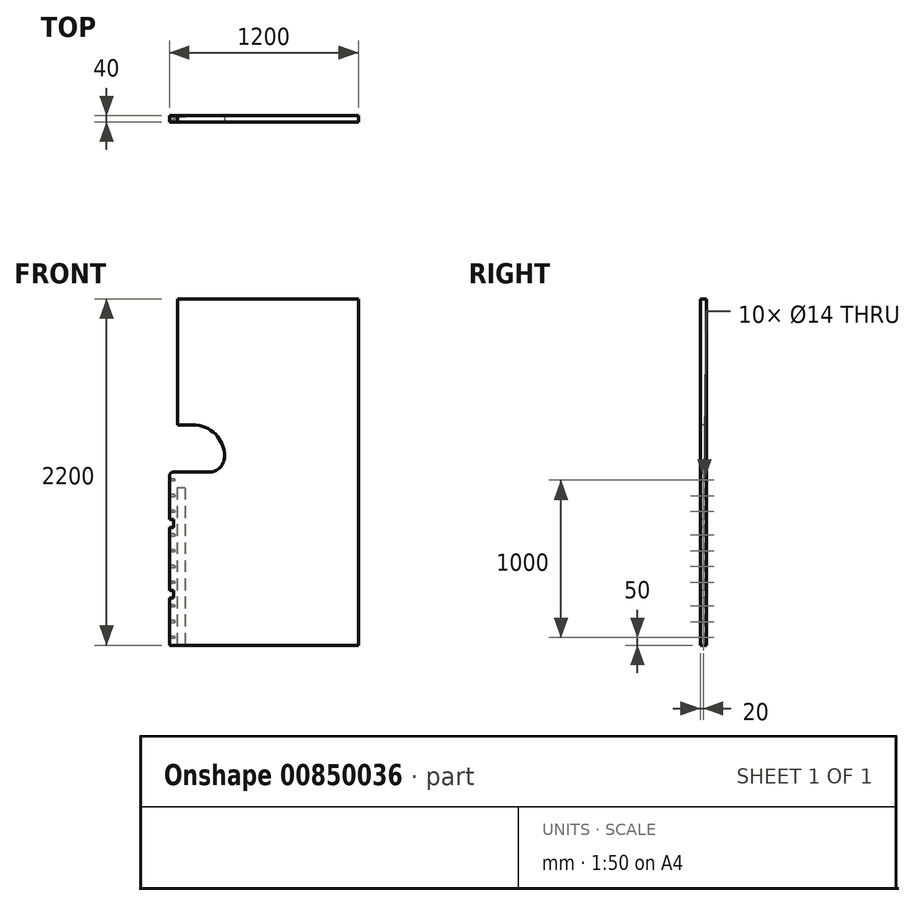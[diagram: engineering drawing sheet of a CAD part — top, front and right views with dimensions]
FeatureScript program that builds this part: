
annotation { "Feature Type Name" : "Feature", "Feature Type Description" : "" }
export const myFeature = defineFeature(function(context is Context, id is Id, definition is map)
    precondition{}
    {
        {
            var Q0;
            Q0=qCreatedBy(makeId("Front.planeOp"),FACE);
            var sketch = newSketch(context, id + "F0", { "sketchPlane" : qUnion([Q0])});
            skLineSegment(sketch, "E0.bottom", {"start": v(600, 1100) * mm, "end": v(-600, 1100) * mm});
            skLineSegment(sketch, "E0.top", {"start": v(600, -1100) * mm, "end": v(-600, -1100) * mm});
            skLineSegment(sketch, "E0.left", {"start": v(600, 1100) * mm, "end": v(600, -1100) * mm});
            skLineSegment(sketch, "E0.right", {"start": v(-600, 1100) * mm, "end": v(-600, -1100) * mm});
            skPoint(sketch, "E0.middle", {"position": v(0, 0) * mm});
            skSolve(sketch);
        }
        {
            var Q0;
            Q0=makeQuery(id+"F0.imprint","IMPRINT",FACE,{"disambiguationData":[TD([[makeQuery(id+"F0.imprint","IMPRINT",EDGE,{"derivedFrom":sQuery(id+"F0.wireOp",EDGE,"E0.bottom")}),1.0]])]});
            extrude(context, id + "F1", {"entities" : qUnion([Q0]), "depth" : 40 * mm, "offsetDistance" : 25 * mm});
        }
        {
            var Q0;
            Q0=makeQuery(id+"F1.opExtrude","CAP_FACE",FACE,{"disambiguationData":[OSD([sQuery(id+"F0.wireOp",EDGE,"E0.bottom"),sQuery(id+"F0.wireOp",EDGE,"E0.top"),sQuery(id+"F0.wireOp",EDGE,"E0.left"),sQuery(id+"F0.wireOp",EDGE,"E0.right")])],"isStart":true});
            var sketch = newSketch(context, id + "F2", { "sketchPlane" : qUnion([Q0])});
            skLineSegment(sketch, "E1.bottom", {"start": v(500, -100) * mm, "end": v(550, -100) * mm});
            skLineSegment(sketch, "E1.top", {"start": v(500, -1100) * mm, "end": v(550, -1100) * mm});
            skLineSegment(sketch, "E1.left", {"start": v(500, -100) * mm, "end": v(500, -1100) * mm});
            skLineSegment(sketch, "E1.right", {"start": v(550, -100) * mm, "end": v(550, -1100) * mm});
            skPoint(sketch, "E2.visualSharp", {"position": v(500, -100) * mm});
            skPoint(sketch, "E3.visualSharp", {"position": v(550, -100) * mm});
            skSolve(sketch);
        }
        {
            var Q0;
            Q0=makeQuery(id+"F2.imprint","IMPRINT",FACE,{"disambiguationData":[TD([[makeQuery(id+"F2.imprint","IMPRINT",EDGE,{"derivedFrom":sQuery(id+"F2.wireOp",EDGE,"E1.bottom")}),-1.0]])]});
            extrude(context, id + "F3", {"entities" : qUnion([Q0]), "operationType" : NewBodyOperationType.REMOVE, "oppositeDirection" : true, "depth" : 10 * mm, "offsetDistance" : 25 * mm});
        }
        {
            var Q0;
            Q0=makeQuery(id+"F1.opExtrude","CAP_FACE",FACE,{"disambiguationData":[OSD([sQuery(id+"F0.wireOp",EDGE,"E0.bottom"),sQuery(id+"F0.wireOp",EDGE,"E0.top"),sQuery(id+"F0.wireOp",EDGE,"E0.left"),sQuery(id+"F0.wireOp",EDGE,"E0.right")])],"isStart":false});
            var sketch = newSketch(context, id + "F4", { "sketchPlane" : qUnion([Q0])});
            skLineSegment(sketch, "E4", {"start": v(-600, 0) * mm, "end": v(-350, 0) * mm});
            skLineSegment(sketch, "E5", {"start": v(-450, 300) * mm, "end": v(-600, 300) * mm});
            skLineSegment(sketch, "E6", {"start": v(-600, 300) * mm, "end": v(-600, 0) * mm});
            skLineSegment(sketch, "E7", {"start": v(-250, 100) * mm, "end": v(-250, 100) * mm});
            skPoint(sketch, "E8.visualSharp", {"position": v(-250, 0) * mm});
            skArc(sketch, "E8.filletArc", {"start": v(-350, 0) * mm, "mid": v(-279.29, 29.29) * mm, "end": v(-250, 100) * mm});
            skPoint(sketch, "E9.visualSharp", {"position": v(-250, 300) * mm});
            skArc(sketch, "E9.filletArc", {"start": v(-250, 100) * mm, "mid": v(-308.58, 241.42) * mm, "end": v(-450, 300) * mm});
            skSolve(sketch);
        }
        {
            var Q0;
            Q0=makeQuery(id+"F4.imprint","IMPRINT",FACE,{"disambiguationData":[TD([[makeQuery(id+"F4.imprint","IMPRINT",EDGE,{"derivedFrom":sQuery(id+"F4.wireOp",EDGE,"E5")}),1.0]])]});
            extrude(context, id + "F5", {"entities" : qUnion([Q0]), "operationType" : NewBodyOperationType.REMOVE, "endBound" : BoundingType.THROUGH_ALL, "oppositeDirection" : true, "depth" : 25 * mm, "offsetDistance" : 25 * mm});
        }
        {
            var Q0;
            Q0=makeQuery(id+"F5.boolean.opBoolean","COPY",EDGE,{"derivedFrom":makeQuery(id+"F5.opExtrude","SWEPT_EDGE",EDGE,{"disambiguationData":[OSD([sQuery(id+"F0.wireOp",EDGE,"E0.right"),sQuery(id+"F4.wireOp",EDGE,"E5"),sQuery(id+"F4.wireOp",EDGE,"E6")])]})});
            var Q1;
            Q1=makeQuery(id+"F5.boolean.opBoolean","COPY",EDGE,{"derivedFrom":makeQuery(id+"F5.opExtrude","SWEPT_EDGE",EDGE,{"disambiguationData":[OSD([sQuery(id+"F0.wireOp",EDGE,"E0.right"),sQuery(id+"F4.wireOp",EDGE,"E4"),sQuery(id+"F4.wireOp",EDGE,"E6")])]})});
            fillet(context, id + "F6", {"entities" : qUnion([Q0, Q1]), "radius" : 25 * mm, "tangentPropagation" : true, "allowEdgeOverflow" : false});
        }
        {
            var Q0;
            Q0=makeQuery(id+"F1.opExtrude","CAP_FACE",FACE,{"disambiguationData":[OSD([sQuery(id+"F0.wireOp",EDGE,"E0.bottom"),sQuery(id+"F0.wireOp",EDGE,"E0.top"),sQuery(id+"F0.wireOp",EDGE,"E0.left"),sQuery(id+"F0.wireOp",EDGE,"E0.right")])],"isStart":false});
            var sketch = newSketch(context, id + "F7", { "sketchPlane" : qUnion([Q0])});
            skLineSegment(sketch, "E10.bottom", {"start": v(-600, 1100) * mm, "end": v(-549.1, 1100) * mm});
            skLineSegment(sketch, "E10.top", {"start": v(-600, 293.93) * mm, "end": v(-549.1, 293.93) * mm});
            skLineSegment(sketch, "E10.left", {"start": v(-600, 1100) * mm, "end": v(-600, 293.93) * mm});
            skLineSegment(sketch, "E10.right", {"start": v(-549.1, 1100) * mm, "end": v(-549.1, 293.93) * mm});
            skSolve(sketch);
        }
        {
            var Q0;
            {var subQ1=sQuery(id+"F7.wireOp",EDGE,"E10.bottom");Q0=makeQuery(id+"F7.imprint","IMPRINT",FACE,{"disambiguationData":[TD([[makeQuery(id+"F7.imprint","IMPRINT",EDGE,{"derivedFrom":subQ1}),1.0]])]});}
            extrude(context, id + "F8", {"entities" : qUnion([Q0]), "operationType" : NewBodyOperationType.REMOVE, "endBound" : BoundingType.THROUGH_ALL, "oppositeDirection" : true, "depth" : 25 * mm, "offsetDistance" : 25 * mm});
        }
        {
            var Q0;
            Q0=makeQuery(id+"F1.opExtrude","CAP_FACE",FACE,{"disambiguationData":[OSD([sQuery(id+"F0.wireOp",EDGE,"E0.bottom"),sQuery(id+"F0.wireOp",EDGE,"E0.top"),sQuery(id+"F0.wireOp",EDGE,"E0.left"),sQuery(id+"F0.wireOp",EDGE,"E0.right")])],"isStart":false});
            var sketch = newSketch(context, id + "F9", { "sketchPlane" : qUnion([Q0])});
            skLineSegment(sketch, "E11.bottom", {"start": v(-600, -300) * mm, "end": v(-575, -300) * mm});
            skLineSegment(sketch, "E11.top", {"start": v(-600, -350) * mm, "end": v(-575, -350) * mm});
            skLineSegment(sketch, "E11.left", {"start": v(-600, -300) * mm, "end": v(-600, -350) * mm});
            skLineSegment(sketch, "E11.right", {"start": v(-575, -300) * mm, "end": v(-575, -350) * mm});
            skLineSegment(sketch, "E12.bottom", {"start": v(-600, -750) * mm, "end": v(-575, -750) * mm});
            skLineSegment(sketch, "E12.top", {"start": v(-600, -800) * mm, "end": v(-575, -800) * mm});
            skLineSegment(sketch, "E12.left", {"start": v(-600, -750) * mm, "end": v(-600, -800) * mm});
            skLineSegment(sketch, "E12.right", {"start": v(-575, -750) * mm, "end": v(-575, -800) * mm});
            skSolve(sketch);
        }
        {
            var Q0;
            Q0=makeQuery(id+"F9.imprint","IMPRINT",FACE,{"disambiguationData":[TD([[makeQuery(id+"F9.imprint","IMPRINT",EDGE,{"derivedFrom":sQuery(id+"F9.wireOp",EDGE,"E11.bottom")}),-1.0]])]});
            var Q1;
            Q1=makeQuery(id+"F9.imprint","IMPRINT",FACE,{"disambiguationData":[TD([[makeQuery(id+"F9.imprint","IMPRINT",EDGE,{"derivedFrom":sQuery(id+"F9.wireOp",EDGE,"E12.bottom")}),-1.0]])]});
            extrude(context, id + "F10", {"entities" : qUnion([Q0, Q1]), "operationType" : NewBodyOperationType.REMOVE, "endBound" : BoundingType.THROUGH_ALL, "oppositeDirection" : true, "depth" : 25 * mm, "offsetDistance" : 25 * mm});
        }
        {
            var Q0;
            {var subQ0=sQuery(id+"F0.wireOp",EDGE,"E0.right");var subQ2=sQuery(id+"F0.wireOp",EDGE,"E0.top");var subQ6=makeQuery(id+"F1.opExtrude","SWEPT_FACE",FACE,{"disambiguationData":[OSD([subQ2])]});Q0=makeQuery(id+"F10.boolean.opBoolean","SPLIT",FACE,{"disambiguationData":[TD([subQ6])],"derivedFrom":makeQuery(id+"F5.boolean.opBoolean","SPLIT",FACE,{"disambiguationData":[TD([subQ6])],"derivedFrom":makeQuery(id+"F1.opExtrude","SWEPT_FACE",FACE,{"disambiguationData":[OSD([subQ0])]})})});}
            var sketch = newSketch(context, id + "F11", { "sketchPlane" : qUnion([Q0])});
            skCircle(sketch, "E13", {"center": v(20, -1050) * mm, "radius": 5 * mm});
            skPoint(sketch, "E13.centerSnap0", {"position": v(20, -1100) * mm});
            skCircle(sketch, "E14", {"center": v(20, -950) * mm, "radius": 5 * mm});
            skCircle(sketch, "E15", {"center": v(20, -850) * mm, "radius": 5 * mm});
            skCircle(sketch, "E16", {"center": v(20, -700) * mm, "radius": 5 * mm});
            skCircle(sketch, "E17", {"center": v(20, -600) * mm, "radius": 5 * mm});
            skCircle(sketch, "E18", {"center": v(20, -500) * mm, "radius": 5 * mm});
            skCircle(sketch, "E19", {"center": v(20, -400) * mm, "radius": 5 * mm});
            skCircle(sketch, "E20", {"center": v(20, -250) * mm, "radius": 5 * mm});
            skCircle(sketch, "E21", {"center": v(20, -150) * mm, "radius": 5 * mm});
            skCircle(sketch, "E22", {"center": v(20, -50) * mm, "radius": 5 * mm});
            skSolve(sketch);
        }
        {
            var Q0;
            Q0=sQuery(id+"F11.wireOp",VERTEX,"E13.center");
            var Q1;
            Q1=sQuery(id+"F11.wireOp",VERTEX,"E14.center");
            var Q2;
            Q2=sQuery(id+"F11.wireOp",VERTEX,"E15.center");
            var Q3;
            Q3=sQuery(id+"F11.wireOp",VERTEX,"E16.center");
            var Q4;
            Q4=sQuery(id+"F11.wireOp",VERTEX,"E17.center");
            var Q5;
            Q5=sQuery(id+"F11.wireOp",VERTEX,"E18.center");
            var Q6;
            Q6=sQuery(id+"F11.wireOp",VERTEX,"E19.center");
            var Q7;
            Q7=sQuery(id+"F11.wireOp",VERTEX,"E20.center");
            var Q8;
            Q8=sQuery(id+"F11.wireOp",VERTEX,"E21.center");
            var Q9;
            Q9=sQuery(id+"F11.wireOp",VERTEX,"E22.center");
            var Q10;
            Q10=makeQuery(id+"F1.opExtrude","SWEPT_BODY",BODY,{"disambiguationData":[OSD([sQuery(id+"F0.wireOp",EDGE,"E0.bottom"),sQuery(id+"F0.wireOp",EDGE,"E0.top"),sQuery(id+"F0.wireOp",EDGE,"E0.left"),sQuery(id+"F0.wireOp",EDGE,"E0.right")])]});
            hole(context, id + "F12", {"style" : HoleStyle.SIMPLE, "endStyle" : HoleEndStyle.BLIND, "standardTappedOrClearance" : lookupTablePath({ "standard" : "ISO", "engagement" : "75%", "pitch" : "2 mm", "size" : "M16", "type" : "Tapped" }), "standardBlindInLast" : lookupTablePath({ "standard" : "ISO", "fit" : "Normal", "engagement" : "75%", "pitch" : "2 mm", "size" : "M16", "type" : "Clearance & tapped" }), "holeDiameter" : 14 * mm, "majorDiameter" : 16 * mm, "showTappedDepth" : true, "holeDepth" : 31 * mm, "tappedDepth" : 25 * mm, "tapClearance" : 3, "startFromSketch" : true, "locations" : qUnion([Q0, Q1, Q2, Q3, Q4, Q5, Q6, Q7, Q8, Q9]), "scope" : qUnion([Q10])});
        }
    });
